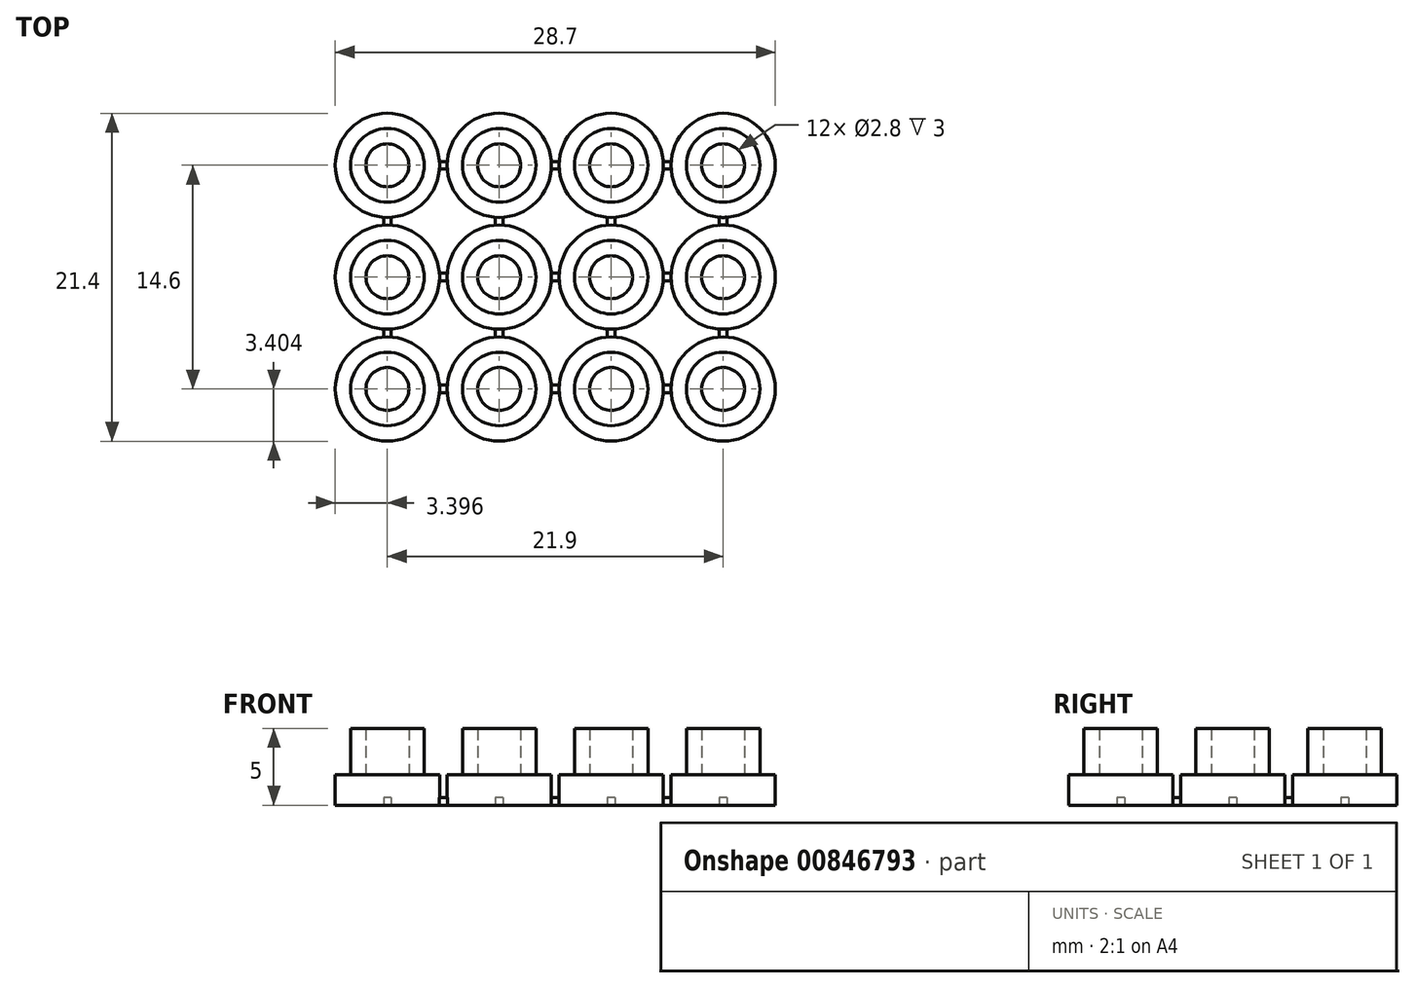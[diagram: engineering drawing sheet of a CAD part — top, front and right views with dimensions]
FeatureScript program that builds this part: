
annotation { "Feature Type Name" : "Feature", "Feature Type Description" : "" }
export const myFeature = defineFeature(function(context is Context, id is Id, definition is map)
    precondition{}
    {
        {
            var Q0;
            Q0=qCreatedBy(makeId("Top.planeOp"),FACE);
            var sketch = newSketch(context, id + "F0", { "sketchPlane" : qUnion([Q0])});
            skCircle(sketch, "E0", {"center": v(-45.85, 46.62) * mm, "radius": 2.4 * mm});
            skCircle(sketch, "E1", {"center": v(-45.85, 46.62) * mm, "radius": 1.4 * mm});
            skCircle(sketch, "E2", {"center": v(-45.85, 46.62) * mm, "radius": 3.4 * mm});
            skCircle(sketch, "E3.0.1.0", {"center": v(-45.85, 53.92) * mm, "radius": 3.4 * mm});
            skCircle(sketch, "E3.0.1.1", {"center": v(-45.85, 53.92) * mm, "radius": 1.4 * mm});
            skCircle(sketch, "E3.0.1.2", {"center": v(-45.85, 53.92) * mm, "radius": 2.4 * mm});
            skCircle(sketch, "E3.0.2.0", {"center": v(-45.85, 61.22) * mm, "radius": 3.4 * mm});
            skCircle(sketch, "E3.0.2.1", {"center": v(-45.85, 61.22) * mm, "radius": 1.4 * mm});
            skCircle(sketch, "E3.0.2.2", {"center": v(-45.85, 61.22) * mm, "radius": 2.4 * mm});
            skCircle(sketch, "E3.1.0.0", {"center": v(-38.55, 46.62) * mm, "radius": 3.4 * mm});
            skCircle(sketch, "E3.1.0.1", {"center": v(-38.55, 46.62) * mm, "radius": 1.4 * mm});
            skCircle(sketch, "E3.1.0.2", {"center": v(-38.55, 46.62) * mm, "radius": 2.4 * mm});
            skCircle(sketch, "E3.1.1.0", {"center": v(-38.55, 53.92) * mm, "radius": 3.4 * mm});
            skCircle(sketch, "E3.1.1.1", {"center": v(-38.55, 53.92) * mm, "radius": 1.4 * mm});
            skCircle(sketch, "E3.1.1.2", {"center": v(-38.55, 53.92) * mm, "radius": 2.4 * mm});
            skCircle(sketch, "E3.1.2.0", {"center": v(-38.55, 61.22) * mm, "radius": 3.4 * mm});
            skCircle(sketch, "E3.1.2.1", {"center": v(-38.55, 61.22) * mm, "radius": 1.4 * mm});
            skCircle(sketch, "E3.1.2.2", {"center": v(-38.55, 61.22) * mm, "radius": 2.4 * mm});
            skCircle(sketch, "E3.2.0.0", {"center": v(-31.25, 46.62) * mm, "radius": 3.4 * mm});
            skCircle(sketch, "E3.2.0.1", {"center": v(-31.25, 46.62) * mm, "radius": 1.4 * mm});
            skCircle(sketch, "E3.2.0.2", {"center": v(-31.25, 46.62) * mm, "radius": 2.4 * mm});
            skCircle(sketch, "E3.2.1.0", {"center": v(-31.25, 53.92) * mm, "radius": 3.4 * mm});
            skCircle(sketch, "E3.2.1.1", {"center": v(-31.25, 53.92) * mm, "radius": 1.4 * mm});
            skCircle(sketch, "E3.2.1.2", {"center": v(-31.25, 53.92) * mm, "radius": 2.4 * mm});
            skCircle(sketch, "E3.2.2.0", {"center": v(-31.25, 61.22) * mm, "radius": 3.4 * mm});
            skCircle(sketch, "E3.2.2.1", {"center": v(-31.25, 61.22) * mm, "radius": 1.4 * mm});
            skCircle(sketch, "E3.2.2.2", {"center": v(-31.25, 61.22) * mm, "radius": 2.4 * mm});
            skCircle(sketch, "E3.3.0.0", {"center": v(-23.95, 46.62) * mm, "radius": 3.4 * mm});
            skCircle(sketch, "E3.3.0.1", {"center": v(-23.95, 46.62) * mm, "radius": 1.4 * mm});
            skCircle(sketch, "E3.3.0.2", {"center": v(-23.95, 46.62) * mm, "radius": 2.4 * mm});
            skCircle(sketch, "E3.3.1.0", {"center": v(-23.95, 53.92) * mm, "radius": 3.4 * mm});
            skCircle(sketch, "E3.3.1.1", {"center": v(-23.95, 53.92) * mm, "radius": 1.4 * mm});
            skCircle(sketch, "E3.3.1.2", {"center": v(-23.95, 53.92) * mm, "radius": 2.4 * mm});
            skCircle(sketch, "E3.3.2.0", {"center": v(-23.95, 61.22) * mm, "radius": 3.4 * mm});
            skCircle(sketch, "E3.3.2.1", {"center": v(-23.95, 61.22) * mm, "radius": 1.4 * mm});
            skCircle(sketch, "E3.3.2.2", {"center": v(-23.95, 61.22) * mm, "radius": 2.4 * mm});
            skLineSegment(sketch, "E3.direction1", {"start": v(-45.85, 46.62) * mm, "end": v(-38.55, 46.62) * mm, "construction": true});
            skLineSegment(sketch, "E3.direction2", {"start": v(-45.85, 46.62) * mm, "end": v(-45.85, 53.92) * mm, "construction": true});
            skPoint(sketch, "E4", {"position": v(-45.85, 57.82) * mm});
            skPoint(sketch, "E5", {"position": v(-45.85, 57.32) * mm});
            skPoint(sketch, "E6", {"position": v(-45.85, 57.57) * mm});
            skLineSegment(sketch, "E7.left", {"start": v(-45.6, 57.31) * mm, "end": v(-45.6, 57.83) * mm});
            skLineSegment(sketch, "E7.right", {"start": v(-46.1, 57.31) * mm, "end": v(-46.1, 57.83) * mm});
            skLineSegment(sketch, "E8.0.1.0", {"start": v(-46.1, 50.01) * mm, "end": v(-46.1, 50.53) * mm});
            skLineSegment(sketch, "E8.0.1.1", {"start": v(-45.6, 50.01) * mm, "end": v(-45.6, 50.53) * mm});
            skLineSegment(sketch, "E8.1.0.0", {"start": v(-38.8, 57.31) * mm, "end": v(-38.8, 57.83) * mm});
            skLineSegment(sketch, "E8.1.0.1", {"start": v(-38.3, 57.31) * mm, "end": v(-38.3, 57.83) * mm});
            skLineSegment(sketch, "E8.1.1.0", {"start": v(-38.8, 50.01) * mm, "end": v(-38.8, 50.53) * mm});
            skLineSegment(sketch, "E8.1.1.1", {"start": v(-38.3, 50.01) * mm, "end": v(-38.3, 50.53) * mm});
            skLineSegment(sketch, "E8.2.0.0", {"start": v(-31.5, 57.31) * mm, "end": v(-31.5, 57.83) * mm});
            skLineSegment(sketch, "E8.2.0.1", {"start": v(-31, 57.31) * mm, "end": v(-31, 57.83) * mm});
            skLineSegment(sketch, "E8.2.1.0", {"start": v(-31.5, 50.01) * mm, "end": v(-31.5, 50.53) * mm});
            skLineSegment(sketch, "E8.2.1.1", {"start": v(-31, 50.01) * mm, "end": v(-31, 50.53) * mm});
            skLineSegment(sketch, "E8.3.0.0", {"start": v(-24.2, 57.31) * mm, "end": v(-24.2, 57.83) * mm});
            skLineSegment(sketch, "E8.3.0.1", {"start": v(-23.7, 57.31) * mm, "end": v(-23.7, 57.83) * mm});
            skLineSegment(sketch, "E8.3.1.0", {"start": v(-24.2, 50.01) * mm, "end": v(-24.2, 50.53) * mm});
            skLineSegment(sketch, "E8.3.1.1", {"start": v(-23.7, 50.01) * mm, "end": v(-23.7, 50.53) * mm});
            skLineSegment(sketch, "E8.direction1", {"start": v(-46.1, 57.31) * mm, "end": v(-38.8, 57.31) * mm, "construction": true});
            skLineSegment(sketch, "E8.direction2", {"start": v(-46.1, 57.31) * mm, "end": v(-46.1, 50.01) * mm, "construction": true});
            skPoint(sketch, "E9", {"position": v(-42.45, 61.22) * mm});
            skPoint(sketch, "E10", {"position": v(-41.95, 61.22) * mm});
            skPoint(sketch, "E11", {"position": v(-42.2, 61.22) * mm});
            skLineSegment(sketch, "E12.bottom", {"start": v(-41.94, 60.97) * mm, "end": v(-42.46, 60.97) * mm});
            skLineSegment(sketch, "E12.top", {"start": v(-41.94, 61.48) * mm, "end": v(-42.46, 61.48) * mm});
            skLineSegment(sketch, "E13.0.1.0", {"start": v(-41.94, 53.67) * mm, "end": v(-42.46, 53.67) * mm});
            skLineSegment(sketch, "E13.0.1.1", {"start": v(-41.94, 54.18) * mm, "end": v(-42.46, 54.18) * mm});
            skLineSegment(sketch, "E13.0.2.0", {"start": v(-41.94, 46.37) * mm, "end": v(-42.46, 46.37) * mm});
            skLineSegment(sketch, "E13.0.2.1", {"start": v(-41.94, 46.88) * mm, "end": v(-42.46, 46.88) * mm});
            skLineSegment(sketch, "E13.1.0.0", {"start": v(-34.64, 60.97) * mm, "end": v(-35.16, 60.97) * mm});
            skLineSegment(sketch, "E13.1.0.1", {"start": v(-34.64, 61.48) * mm, "end": v(-35.16, 61.48) * mm});
            skLineSegment(sketch, "E13.1.1.0", {"start": v(-34.64, 53.67) * mm, "end": v(-35.16, 53.67) * mm});
            skLineSegment(sketch, "E13.1.1.1", {"start": v(-34.64, 54.18) * mm, "end": v(-35.16, 54.18) * mm});
            skLineSegment(sketch, "E13.1.2.0", {"start": v(-34.64, 46.37) * mm, "end": v(-35.16, 46.37) * mm});
            skLineSegment(sketch, "E13.1.2.1", {"start": v(-34.64, 46.88) * mm, "end": v(-35.16, 46.88) * mm});
            skLineSegment(sketch, "E13.2.0.0", {"start": v(-27.34, 60.97) * mm, "end": v(-27.86, 60.97) * mm});
            skLineSegment(sketch, "E13.2.0.1", {"start": v(-27.34, 61.48) * mm, "end": v(-27.86, 61.48) * mm});
            skLineSegment(sketch, "E13.2.1.0", {"start": v(-27.34, 53.67) * mm, "end": v(-27.86, 53.67) * mm});
            skLineSegment(sketch, "E13.2.1.1", {"start": v(-27.34, 54.18) * mm, "end": v(-27.86, 54.18) * mm});
            skLineSegment(sketch, "E13.2.2.0", {"start": v(-27.34, 46.37) * mm, "end": v(-27.86, 46.37) * mm});
            skLineSegment(sketch, "E13.2.2.1", {"start": v(-27.34, 46.88) * mm, "end": v(-27.86, 46.88) * mm});
            skLineSegment(sketch, "E13.direction1", {"start": v(-42.46, 60.97) * mm, "end": v(-35.16, 60.97) * mm, "construction": true});
            skLineSegment(sketch, "E13.direction2", {"start": v(-42.46, 60.97) * mm, "end": v(-42.46, 53.67) * mm, "construction": true});
            skSolve(sketch);
        }
        {
            var Q0;
            Q0=makeQuery(id+"F0.imprint","IMPRINT",FACE,{"disambiguationData":[TD([[makeQuery(id+"F0.imprint","IMPRINT",EDGE,{"derivedFrom":sQuery(id+"F0.wireOp",EDGE,"E0")}),1.0]])]});
            var Q1;
            Q1=makeQuery(id+"F0.imprint","IMPRINT",FACE,{"disambiguationData":[TD([[makeQuery(id+"F0.imprint","IMPRINT",EDGE,{"derivedFrom":sQuery(id+"F0.wireOp",EDGE,"E3.1.0.1")}),-1.0]])]});
            var Q2;
            Q2=makeQuery(id+"F0.imprint","IMPRINT",FACE,{"disambiguationData":[TD([[makeQuery(id+"F0.imprint","IMPRINT",EDGE,{"derivedFrom":sQuery(id+"F0.wireOp",EDGE,"E3.2.0.1")}),-1.0]])]});
            var Q3;
            Q3=makeQuery(id+"F0.imprint","IMPRINT",FACE,{"disambiguationData":[TD([[makeQuery(id+"F0.imprint","IMPRINT",EDGE,{"derivedFrom":sQuery(id+"F0.wireOp",EDGE,"E3.3.0.1")}),-1.0]])]});
            var Q4;
            Q4=makeQuery(id+"F0.imprint","IMPRINT",FACE,{"disambiguationData":[TD([[makeQuery(id+"F0.imprint","IMPRINT",EDGE,{"derivedFrom":sQuery(id+"F0.wireOp",EDGE,"E3.3.1.1")}),-1.0]])]});
            var Q5;
            Q5=makeQuery(id+"F0.imprint","IMPRINT",FACE,{"disambiguationData":[TD([[makeQuery(id+"F0.imprint","IMPRINT",EDGE,{"derivedFrom":sQuery(id+"F0.wireOp",EDGE,"E3.2.1.1")}),-1.0]])]});
            var Q6;
            Q6=makeQuery(id+"F0.imprint","IMPRINT",FACE,{"disambiguationData":[TD([[makeQuery(id+"F0.imprint","IMPRINT",EDGE,{"derivedFrom":sQuery(id+"F0.wireOp",EDGE,"E3.1.1.1")}),-1.0]])]});
            var Q7;
            Q7=makeQuery(id+"F0.imprint","IMPRINT",FACE,{"disambiguationData":[TD([[makeQuery(id+"F0.imprint","IMPRINT",EDGE,{"derivedFrom":sQuery(id+"F0.wireOp",EDGE,"E3.0.1.1")}),-1.0]])]});
            var Q8;
            Q8=makeQuery(id+"F0.imprint","IMPRINT",FACE,{"disambiguationData":[TD([[makeQuery(id+"F0.imprint","IMPRINT",EDGE,{"derivedFrom":sQuery(id+"F0.wireOp",EDGE,"E3.0.2.1")}),-1.0]])]});
            var Q9;
            Q9=makeQuery(id+"F0.imprint","IMPRINT",FACE,{"disambiguationData":[TD([[makeQuery(id+"F0.imprint","IMPRINT",EDGE,{"derivedFrom":sQuery(id+"F0.wireOp",EDGE,"E3.1.2.1")}),-1.0]])]});
            var Q10;
            Q10=makeQuery(id+"F0.imprint","IMPRINT",FACE,{"disambiguationData":[TD([[makeQuery(id+"F0.imprint","IMPRINT",EDGE,{"derivedFrom":sQuery(id+"F0.wireOp",EDGE,"E3.2.2.1")}),-1.0]])]});
            var Q11;
            Q11=makeQuery(id+"F0.imprint","IMPRINT",FACE,{"disambiguationData":[TD([[makeQuery(id+"F0.imprint","IMPRINT",EDGE,{"derivedFrom":sQuery(id+"F0.wireOp",EDGE,"E3.3.2.1")}),-1.0]])]});
            extrude(context, id + "F1", {"entities" : qUnion([Q0, Q1, Q2, Q3, Q4, Q5, Q6, Q7, Q8, Q9, Q10, Q11]), "depth" : 5 * mm, "offsetDistance" : 25 * mm});
        }
        {
            var Q0;
            Q0=makeQuery(id+"F0.imprint","IMPRINT",FACE,{"disambiguationData":[TD([[makeQuery(id+"F0.imprint","IMPRINT",EDGE,{"derivedFrom":sQuery(id+"F0.wireOp",EDGE,"E0")}),-1.0]])]});
            var Q1;
            Q1=makeQuery(id+"F0.imprint","IMPRINT",FACE,{"disambiguationData":[TD([[makeQuery(id+"F0.imprint","IMPRINT",EDGE,{"derivedFrom":sQuery(id+"F0.wireOp",EDGE,"E1")}),1.0]])]});
            var Q2;
            Q2=makeQuery(id+"F0.imprint","IMPRINT",FACE,{"disambiguationData":[TD([[makeQuery(id+"F0.imprint","IMPRINT",EDGE,{"derivedFrom":sQuery(id+"F0.wireOp",EDGE,"E3.1.0.0")}),1.0]])]});
            var Q3;
            Q3=makeQuery(id+"F0.imprint","IMPRINT",FACE,{"disambiguationData":[TD([[makeQuery(id+"F0.imprint","IMPRINT",EDGE,{"derivedFrom":sQuery(id+"F0.wireOp",EDGE,"E3.2.0.0")}),1.0]])]});
            var Q4;
            Q4=makeQuery(id+"F0.imprint","IMPRINT",FACE,{"disambiguationData":[TD([[makeQuery(id+"F0.imprint","IMPRINT",EDGE,{"derivedFrom":sQuery(id+"F0.wireOp",EDGE,"E3.2.0.1")}),1.0]])]});
            var Q5;
            Q5=makeQuery(id+"F0.imprint","IMPRINT",FACE,{"disambiguationData":[TD([[makeQuery(id+"F0.imprint","IMPRINT",EDGE,{"derivedFrom":sQuery(id+"F0.wireOp",EDGE,"E3.3.0.1")}),1.0]])]});
            var Q6;
            Q6=makeQuery(id+"F0.imprint","IMPRINT",FACE,{"disambiguationData":[TD([[makeQuery(id+"F0.imprint","IMPRINT",EDGE,{"derivedFrom":sQuery(id+"F0.wireOp",EDGE,"E3.1.0.1")}),1.0]])]});
            var Q7;
            Q7=makeQuery(id+"F0.imprint","IMPRINT",FACE,{"disambiguationData":[TD([[makeQuery(id+"F0.imprint","IMPRINT",EDGE,{"derivedFrom":sQuery(id+"F0.wireOp",EDGE,"E3.3.1.0")}),1.0]])]});
            var Q8;
            Q8=makeQuery(id+"F0.imprint","IMPRINT",FACE,{"disambiguationData":[TD([[makeQuery(id+"F0.imprint","IMPRINT",EDGE,{"derivedFrom":sQuery(id+"F0.wireOp",EDGE,"E3.3.1.1")}),1.0]])]});
            var Q9;
            Q9=makeQuery(id+"F0.imprint","IMPRINT",FACE,{"disambiguationData":[TD([[makeQuery(id+"F0.imprint","IMPRINT",EDGE,{"derivedFrom":sQuery(id+"F0.wireOp",EDGE,"E3.2.1.0")}),1.0]])]});
            var Q10;
            Q10=makeQuery(id+"F0.imprint","IMPRINT",FACE,{"disambiguationData":[TD([[makeQuery(id+"F0.imprint","IMPRINT",EDGE,{"derivedFrom":sQuery(id+"F0.wireOp",EDGE,"E3.3.0.0")}),1.0]])]});
            var Q11;
            Q11=makeQuery(id+"F0.imprint","IMPRINT",FACE,{"disambiguationData":[TD([[makeQuery(id+"F0.imprint","IMPRINT",EDGE,{"derivedFrom":sQuery(id+"F0.wireOp",EDGE,"E3.2.1.1")}),1.0]])]});
            var Q12;
            Q12=makeQuery(id+"F0.imprint","IMPRINT",FACE,{"disambiguationData":[TD([[makeQuery(id+"F0.imprint","IMPRINT",EDGE,{"derivedFrom":sQuery(id+"F0.wireOp",EDGE,"E3.1.1.0")}),1.0]])]});
            var Q13;
            Q13=makeQuery(id+"F0.imprint","IMPRINT",FACE,{"disambiguationData":[TD([[makeQuery(id+"F0.imprint","IMPRINT",EDGE,{"derivedFrom":sQuery(id+"F0.wireOp",EDGE,"E3.1.1.1")}),1.0]])]});
            var Q14;
            Q14=makeQuery(id+"F0.imprint","IMPRINT",FACE,{"disambiguationData":[TD([[makeQuery(id+"F0.imprint","IMPRINT",EDGE,{"derivedFrom":sQuery(id+"F0.wireOp",EDGE,"E3.0.1.0")}),1.0]])]});
            var Q15;
            Q15=makeQuery(id+"F0.imprint","IMPRINT",FACE,{"disambiguationData":[TD([[makeQuery(id+"F0.imprint","IMPRINT",EDGE,{"derivedFrom":sQuery(id+"F0.wireOp",EDGE,"E3.0.1.1")}),1.0]])]});
            var Q16;
            Q16=makeQuery(id+"F0.imprint","IMPRINT",FACE,{"disambiguationData":[TD([[makeQuery(id+"F0.imprint","IMPRINT",EDGE,{"derivedFrom":sQuery(id+"F0.wireOp",EDGE,"E3.0.2.0")}),1.0]])]});
            var Q17;
            Q17=makeQuery(id+"F0.imprint","IMPRINT",FACE,{"disambiguationData":[TD([[makeQuery(id+"F0.imprint","IMPRINT",EDGE,{"derivedFrom":sQuery(id+"F0.wireOp",EDGE,"E3.0.2.1")}),1.0]])]});
            var Q18;
            Q18=makeQuery(id+"F0.imprint","IMPRINT",FACE,{"disambiguationData":[TD([[makeQuery(id+"F0.imprint","IMPRINT",EDGE,{"derivedFrom":sQuery(id+"F0.wireOp",EDGE,"E3.1.2.0")}),1.0]])]});
            var Q19;
            Q19=makeQuery(id+"F0.imprint","IMPRINT",FACE,{"disambiguationData":[TD([[makeQuery(id+"F0.imprint","IMPRINT",EDGE,{"derivedFrom":sQuery(id+"F0.wireOp",EDGE,"E3.1.2.1")}),1.0]])]});
            var Q20;
            Q20=makeQuery(id+"F0.imprint","IMPRINT",FACE,{"disambiguationData":[TD([[makeQuery(id+"F0.imprint","IMPRINT",EDGE,{"derivedFrom":sQuery(id+"F0.wireOp",EDGE,"E3.2.2.0")}),1.0]])]});
            var Q21;
            Q21=makeQuery(id+"F0.imprint","IMPRINT",FACE,{"disambiguationData":[TD([[makeQuery(id+"F0.imprint","IMPRINT",EDGE,{"derivedFrom":sQuery(id+"F0.wireOp",EDGE,"E3.2.2.1")}),1.0]])]});
            var Q22;
            Q22=makeQuery(id+"F0.imprint","IMPRINT",FACE,{"disambiguationData":[TD([[makeQuery(id+"F0.imprint","IMPRINT",EDGE,{"derivedFrom":sQuery(id+"F0.wireOp",EDGE,"E3.3.2.0")}),1.0]])]});
            var Q23;
            Q23=makeQuery(id+"F0.imprint","IMPRINT",FACE,{"disambiguationData":[TD([[makeQuery(id+"F0.imprint","IMPRINT",EDGE,{"derivedFrom":sQuery(id+"F0.wireOp",EDGE,"E3.3.2.1")}),1.0]])]});
            extrude(context, id + "F2", {"entities" : qUnion([Q0, Q1, Q2, Q3, Q4, Q5, Q6, Q7, Q8, Q9, Q10, Q11, Q12, Q13, Q14, Q15, Q16, Q17, Q18, Q19, Q20, Q21, Q22, Q23]), "operationType" : NewBodyOperationType.ADD, "depth" : 2 * mm, "offsetDistance" : 25 * mm});
        }
        {
            var Q0;
            {var subQ0=sQuery(id+"F0.wireOp",EDGE,"E7.left");Q0=makeQuery(id+"F0.imprint","IMPRINT",FACE,{"disambiguationData":[TD([[makeQuery(id+"F0.imprint","IMPRINT",EDGE,{"derivedFrom":subQ0}),1.0]])]});}
            var Q1;
            {var subQ0=sQuery(id+"F0.wireOp",EDGE,"E8.1.0.0");Q1=makeQuery(id+"F0.imprint","IMPRINT",FACE,{"disambiguationData":[TD([[makeQuery(id+"F0.imprint","IMPRINT",EDGE,{"derivedFrom":subQ0}),-1.0]])]});}
            var Q2;
            {var subQ0=sQuery(id+"F0.wireOp",EDGE,"E8.2.0.0");Q2=makeQuery(id+"F0.imprint","IMPRINT",FACE,{"disambiguationData":[TD([[makeQuery(id+"F0.imprint","IMPRINT",EDGE,{"derivedFrom":subQ0}),-1.0]])]});}
            var Q3;
            {var subQ0=sQuery(id+"F0.wireOp",EDGE,"E8.3.0.0");Q3=makeQuery(id+"F0.imprint","IMPRINT",FACE,{"disambiguationData":[TD([[makeQuery(id+"F0.imprint","IMPRINT",EDGE,{"derivedFrom":subQ0}),-1.0]])]});}
            var Q4;
            {var subQ0=sQuery(id+"F0.wireOp",EDGE,"E8.3.1.0");Q4=makeQuery(id+"F0.imprint","IMPRINT",FACE,{"disambiguationData":[TD([[makeQuery(id+"F0.imprint","IMPRINT",EDGE,{"derivedFrom":subQ0}),-1.0]])]});}
            var Q5;
            {var subQ0=sQuery(id+"F0.wireOp",EDGE,"E8.2.1.0");Q5=makeQuery(id+"F0.imprint","IMPRINT",FACE,{"disambiguationData":[TD([[makeQuery(id+"F0.imprint","IMPRINT",EDGE,{"derivedFrom":subQ0}),-1.0]])]});}
            var Q6;
            {var subQ0=sQuery(id+"F0.wireOp",EDGE,"E8.1.1.0");Q6=makeQuery(id+"F0.imprint","IMPRINT",FACE,{"disambiguationData":[TD([[makeQuery(id+"F0.imprint","IMPRINT",EDGE,{"derivedFrom":subQ0}),-1.0]])]});}
            var Q7;
            {var subQ0=sQuery(id+"F0.wireOp",EDGE,"E8.0.1.0");Q7=makeQuery(id+"F0.imprint","IMPRINT",FACE,{"disambiguationData":[TD([[makeQuery(id+"F0.imprint","IMPRINT",EDGE,{"derivedFrom":subQ0}),-1.0]])]});}
            var Q8;
            {var subQ0=sQuery(id+"F0.wireOp",EDGE,"E13.0.2.0");Q8=makeQuery(id+"F0.imprint","IMPRINT",FACE,{"disambiguationData":[TD([[makeQuery(id+"F0.imprint","IMPRINT",EDGE,{"derivedFrom":subQ0}),-1.0]])]});}
            var Q9;
            {var subQ0=sQuery(id+"F0.wireOp",EDGE,"E13.0.1.0");Q9=makeQuery(id+"F0.imprint","IMPRINT",FACE,{"disambiguationData":[TD([[makeQuery(id+"F0.imprint","IMPRINT",EDGE,{"derivedFrom":subQ0}),-1.0]])]});}
            var Q10;
            {var subQ0=sQuery(id+"F0.wireOp",EDGE,"E13.1.1.0");Q10=makeQuery(id+"F0.imprint","IMPRINT",FACE,{"disambiguationData":[TD([[makeQuery(id+"F0.imprint","IMPRINT",EDGE,{"derivedFrom":subQ0}),-1.0]])]});}
            var Q11;
            {var subQ0=sQuery(id+"F0.wireOp",EDGE,"E13.2.1.0");Q11=makeQuery(id+"F0.imprint","IMPRINT",FACE,{"disambiguationData":[TD([[makeQuery(id+"F0.imprint","IMPRINT",EDGE,{"derivedFrom":subQ0}),-1.0]])]});}
            var Q12;
            {var subQ0=sQuery(id+"F0.wireOp",EDGE,"E13.2.0.0");Q12=makeQuery(id+"F0.imprint","IMPRINT",FACE,{"disambiguationData":[TD([[makeQuery(id+"F0.imprint","IMPRINT",EDGE,{"derivedFrom":subQ0}),-1.0]])]});}
            var Q13;
            {var subQ0=sQuery(id+"F0.wireOp",EDGE,"E13.1.0.0");Q13=makeQuery(id+"F0.imprint","IMPRINT",FACE,{"disambiguationData":[TD([[makeQuery(id+"F0.imprint","IMPRINT",EDGE,{"derivedFrom":subQ0}),-1.0]])]});}
            var Q14;
            {var subQ0=sQuery(id+"F0.wireOp",EDGE,"E12.bottom");Q14=makeQuery(id+"F0.imprint","IMPRINT",FACE,{"disambiguationData":[TD([[makeQuery(id+"F0.imprint","IMPRINT",EDGE,{"derivedFrom":subQ0}),-1.0]])]});}
            var Q15;
            {var subQ0=sQuery(id+"F0.wireOp",EDGE,"E13.1.2.0");Q15=makeQuery(id+"F0.imprint","IMPRINT",FACE,{"disambiguationData":[TD([[makeQuery(id+"F0.imprint","IMPRINT",EDGE,{"derivedFrom":subQ0}),-1.0]])]});}
            var Q16;
            {var subQ0=sQuery(id+"F0.wireOp",EDGE,"E13.2.2.0");Q16=makeQuery(id+"F0.imprint","IMPRINT",FACE,{"disambiguationData":[TD([[makeQuery(id+"F0.imprint","IMPRINT",EDGE,{"derivedFrom":subQ0}),-1.0]])]});}
            extrude(context, id + "F3", {"entities" : qUnion([Q0, Q1, Q2, Q3, Q4, Q5, Q6, Q7, Q8, Q9, Q10, Q11, Q12, Q13, Q14, Q15, Q16]), "depth" : 0.5 * mm, "offsetDistance" : 25 * mm});
        }
    });
